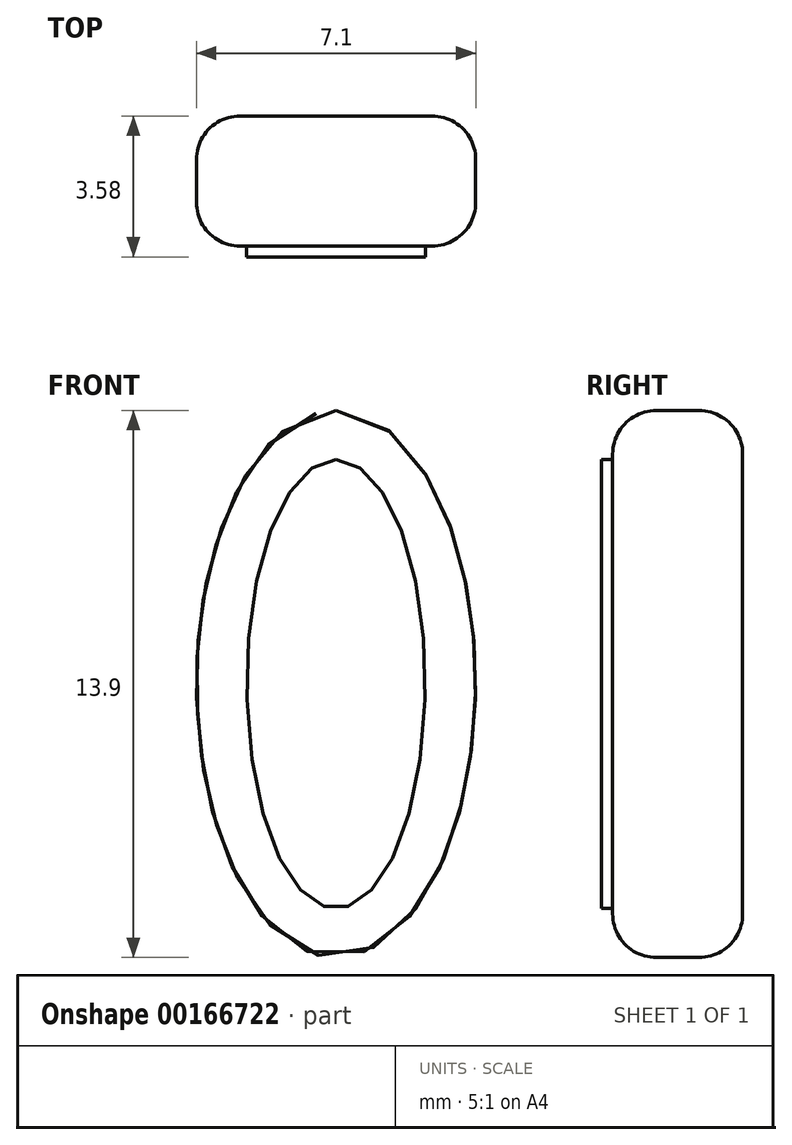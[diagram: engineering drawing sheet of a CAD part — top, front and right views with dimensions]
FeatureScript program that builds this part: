
annotation { "Feature Type Name" : "Feature", "Feature Type Description" : "" }
export const myFeature = defineFeature(function(context is Context, id is Id, definition is map)
    precondition{}
    {
        {
            var Q0;
            Q0=qCreatedBy(makeId("Front.planeOp"),FACE);
            var sketch = newSketch(context, id + "F0", { "sketchPlane" : qUnion([Q0])});
            skEllipse(sketch, "E0", {"center": v(0, 3.3) * mm, "majorRadius": 6.95 * mm, "minorRadius": 3.55 * mm, "majorAxis": v(0, 1)});
            skSolve(sketch);
        }
        {
            var Q0;
            Q0=makeQuery(id+"F0.imprint","IMPRINT",FACE,{"disambiguationData":[TD([[makeQuery(id+"F0.imprint","IMPRINT",EDGE,{"derivedFrom":sQuery(id+"F0.wireOp",EDGE,"E0")}),1.0]])]});
            extrude(context, id + "F1", {"entities" : qUnion([Q0]), "depth" : 3.3 * mm});
        }
        {
            var Q0;
            Q0=makeQuery(id+"F1.opExtrude","CAP_EDGE",EDGE,{"disambiguationData":[OSD([sQuery(id+"F0.wireOp",EDGE,"E0")])],"isStart":false});
            var Q1;
            Q1=makeQuery(id+"F1.opExtrude","CAP_EDGE",EDGE,{"disambiguationData":[OSD([sQuery(id+"F0.wireOp",EDGE,"E0")])],"isStart":true});
            fillet(context, id + "F2", {"entities" : qUnion([Q0, Q1]), "radius" : 1.1 * mm, "tangentPropagation" : true, "allowEdgeOverflow" : false});
        }
        {
            var Q0;
            Q0=qCreatedBy(makeId("Front.planeOp"),FACE);
            var sketch = newSketch(context, id + "F3", { "sketchPlane" : qUnion([Q0])});
            skEllipse(sketch, "E1", {"center": v(0, 3.3) * mm, "majorRadius": 5.7 * mm, "minorRadius": 2.27 * mm, "majorAxis": v(0, 1)});
            skSolve(sketch);
        }
        {
            var Q0;
            Q0 = qSketchRegion(id + "F3", true);
            extrude(context, id + "F4", {"entities" : qUnion([Q0]), "operationType" : NewBodyOperationType.ADD, "depth" : 3.58 * mm});
        }
    });
